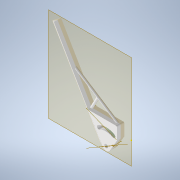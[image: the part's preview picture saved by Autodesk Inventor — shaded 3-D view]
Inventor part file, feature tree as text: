
AUTODESK INVENTOR PART (.ipt)
format: ipt  version: 2020 (Build 240168000, 168)  size: 199,680 bytes
history: native  units: mm
features: sketch x10, other x5, extrude x4, plane x3, reference x3, sweep x2, chamfer x1, fillet x1
ambient origin geometry x8: Origin, YZ Plane, XZ Plane, XY Plane, X Axis, Y Axis, Z Axis, Center Point
bodies: Volumenkörper1 (feature_tree)
feature tree (29):
  extrude  "Extrusion1"  Depth=15.0mm
  extrude  "Extrusion2"  Depth=4.0mm
  extrude  "Extrusion3"  Depth=6.0mm
  other  "Arbeitsachse1"
  other  "Arbeitspunkt1"
  plane  "Arbeitsebene1"
  sketch  "Skizze4"  dims[d9=1.5mm d10=10.0mm d11=0.0mm d12=0.0mm d13=0.0mm]
  sketch  "Skizze5"  dims[d14=3.0mm d15=0.0mm]
  extrude  "Extrusion4"  Depth=10.0mm TaperAngle=0.0deg
  chamfer  "Fase1"  [1 undecoded]
  plane  "Arbeitsebene2"
  sweep  "Sweeping2"
  sketch  "Skizze9"  dims[d24=3.0mm]
  plane  "Arbeitsebene3"
  sweep  "Sweeping3"
  fillet  "Rundung1"  Radius=3.0mm
  sketch  "Skizze1"  dims[d1=4.0mm d2=15.0mm]
  reference  "Referenz1"
  reference  "Referenz2"
  sketch  "Skizze2"  dims[d3=15.0mm d5=4.0mm]
  sketch  "Skizze3"  dims[d6=6.0mm d7=0.0mm d8=27.003mm]
  reference  "Referenz3"
  sketch  "Skizze6"  dims[d16=5.0mm d17=80.0mm d18=0.0mm]
  sketch  "Skizze7"  dims[d19=2.0mm d20=2.0mm d21=45.0deg d22=3.0mm]
  sketch  "Skizze8"  dims[d23=40.0mm]
  sketch  "Skizze10"  dims[d25=2.0mm d28=0.0mm d29=0.0mm d30=2.0mm d31=0.0mm d32=0.0mm d33=1.0mm]
  parser-record x1  (decoder bookkeeping rows leaked as tree rows — omitted from the tree; the rows remain in map.json)
  other  "GlassesAssembly.iam"
  other  "CemaraArmInterface:1"
note: 1 required parameter value undecoded (feature->parameter linkage not recoverable at this tier; creation-order binding heuristic only, values carry confidence <= 0.55)
note: 1 file-system path scrubbed to <path> (originals preserved in map.json)
